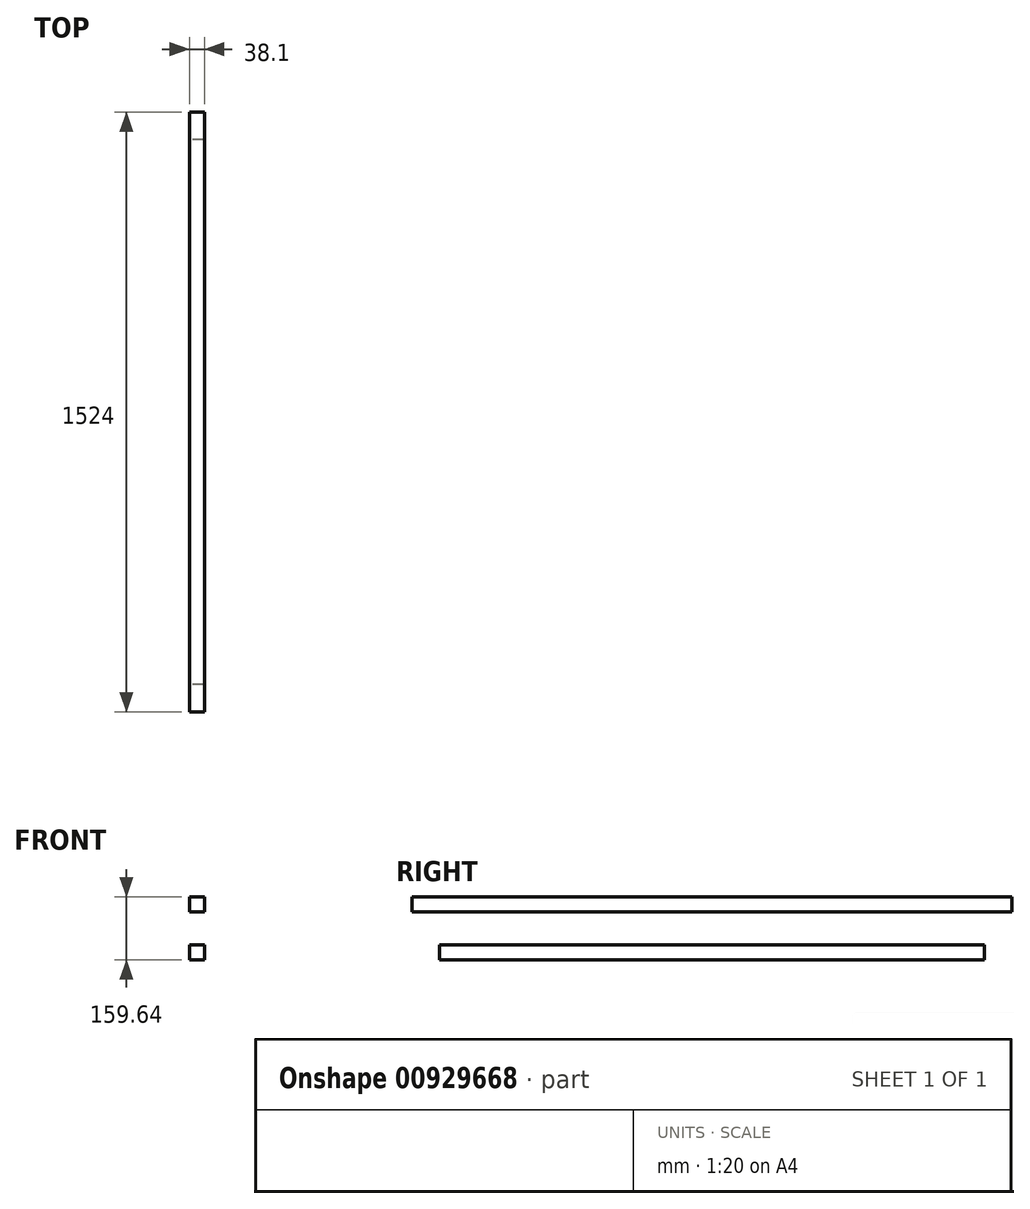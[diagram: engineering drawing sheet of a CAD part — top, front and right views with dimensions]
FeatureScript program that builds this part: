
annotation { "Feature Type Name" : "Feature", "Feature Type Description" : "" }
export const myFeature = defineFeature(function(context is Context, id is Id, definition is map)
    precondition{}
    {
        {
            var Q0;
            Q0=qCreatedBy(makeId("Right.planeOp"),FACE);
            var sketch = newSketch(context, id + "F0", { "sketchPlane" : qUnion([Q0])});
            skLineSegment(sketch, "E0.bottom", {"start": v(692.15, 19.05) * mm, "end": v(-692.15, 19.05) * mm});
            skLineSegment(sketch, "E0.top", {"start": v(692.15, -19.05) * mm, "end": v(-692.15, -19.05) * mm});
            skLineSegment(sketch, "E0.left", {"start": v(692.15, 19.05) * mm, "end": v(692.15, -19.05) * mm});
            skLineSegment(sketch, "E0.right", {"start": v(-692.15, 19.05) * mm, "end": v(-692.15, -19.05) * mm});
            skPoint(sketch, "E0.middle", {"position": v(0, 0) * mm});
            skSolve(sketch);
        }
        {
            var Q0;
            Q0=makeQuery(id+"F0.imprint","IMPRINT",FACE,{"disambiguationData":[TD([[makeQuery(id+"F0.imprint","IMPRINT",EDGE,{"derivedFrom":sQuery(id+"F0.wireOp",EDGE,"E0.bottom")}),1.0]])]});
            extrude(context, id + "F1", {"entities" : qUnion([Q0]), "depth" : 38.1 * mm, "offsetDistance" : 25.4 * mm});
        }
        {
            var Q0;
            Q0=qCreatedBy(makeId("Right.planeOp"),FACE);
            var sketch = newSketch(context, id + "F2", { "sketchPlane" : qUnion([Q0])});
            skLineSegment(sketch, "E1.bottom", {"start": v(762, 140.59) * mm, "end": v(-762, 140.59) * mm});
            skLineSegment(sketch, "E1.top", {"start": v(762, 102.49) * mm, "end": v(-762, 102.49) * mm});
            skLineSegment(sketch, "E1.left", {"start": v(762, 140.59) * mm, "end": v(762, 102.49) * mm});
            skLineSegment(sketch, "E1.right", {"start": v(-762, 140.59) * mm, "end": v(-762, 102.49) * mm});
            skPoint(sketch, "E1.middle", {"position": v(0, 121.54) * mm});
            skSolve(sketch);
        }
        {
            var Q0;
            Q0=makeQuery(id+"F2.imprint","IMPRINT",FACE,{"disambiguationData":[TD([[makeQuery(id+"F2.imprint","IMPRINT",EDGE,{"derivedFrom":sQuery(id+"F2.wireOp",EDGE,"E1.bottom")}),1.0]])]});
            extrude(context, id + "F3", {"entities" : qUnion([Q0]), "depth" : 38.1 * mm, "offsetDistance" : 25.4 * mm});
        }
    });
